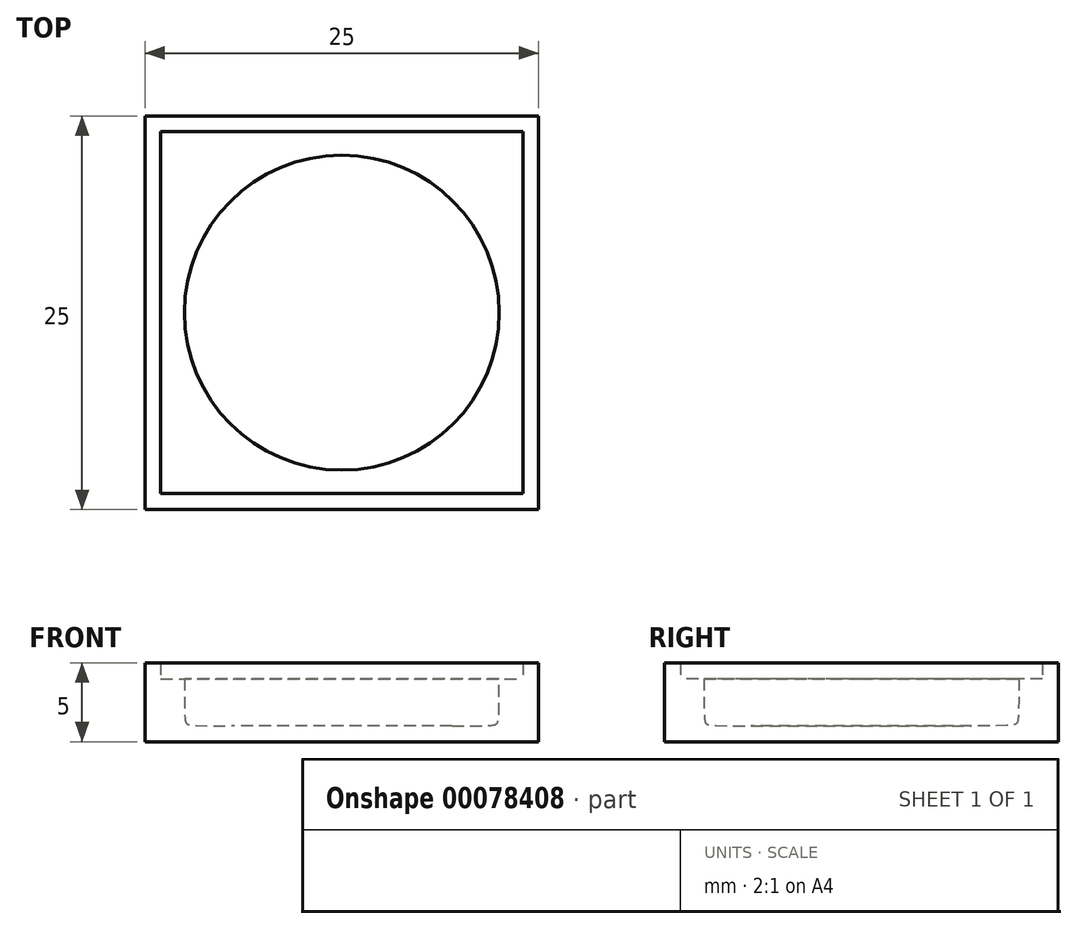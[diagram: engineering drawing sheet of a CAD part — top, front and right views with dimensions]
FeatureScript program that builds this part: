
annotation { "Feature Type Name" : "Feature", "Feature Type Description" : "" }
export const myFeature = defineFeature(function(context is Context, id is Id, definition is map)
    precondition{}
    {
        {
            var Q0;
            Q0=qCreatedBy(makeId("Top.planeOp"),FACE);
            var sketch = newSketch(context, id + "F0", { "sketchPlane" : qUnion([Q0])});
            skLineSegment(sketch, "E0.bottom", {"start": v(-11.5, 11.5) * mm, "end": v(11.5, 11.5) * mm});
            skLineSegment(sketch, "E0.top", {"start": v(-11.5, -11.5) * mm, "end": v(11.5, -11.5) * mm});
            skLineSegment(sketch, "E0.left", {"start": v(-11.5, 11.5) * mm, "end": v(-11.5, -11.5) * mm});
            skLineSegment(sketch, "E0.right", {"start": v(11.5, 11.5) * mm, "end": v(11.5, -11.5) * mm});
            skPoint(sketch, "E0.middle", {"position": v(0, 0) * mm});
            skCircle(sketch, "E1", {"center": v(0, 0) * mm, "radius": 10 * mm});
            skLineSegment(sketch, "E2.bottom", {"start": v(-12.5, 12.5) * mm, "end": v(12.5, 12.5) * mm});
            skLineSegment(sketch, "E2.top", {"start": v(-12.5, -12.5) * mm, "end": v(12.5, -12.5) * mm});
            skLineSegment(sketch, "E2.left", {"start": v(-12.5, 12.5) * mm, "end": v(-12.5, -12.5) * mm});
            skLineSegment(sketch, "E2.right", {"start": v(12.5, 12.5) * mm, "end": v(12.5, -12.5) * mm});
            skSolve(sketch);
        }
        {
            var Q0;
            Q0=makeQuery(id+"F0.imprint","IMPRINT",FACE,{"disambiguationData":[TD([[makeQuery(id+"F0.imprint","IMPRINT",EDGE,{"derivedFrom":sQuery(id+"F0.wireOp",EDGE,"E1")}),1.0]])]});
            var Q1;
            Q1=makeQuery(id+"F0.imprint","IMPRINT",FACE,{"disambiguationData":[TD([[makeQuery(id+"F0.imprint","IMPRINT",EDGE,{"derivedFrom":sQuery(id+"F0.wireOp",EDGE,"E0.bottom")}),-1.0]])]});
            var Q2;
            Q2=makeQuery(id+"F0.imprint","IMPRINT",FACE,{"disambiguationData":[TD([[makeQuery(id+"F0.imprint","IMPRINT",EDGE,{"derivedFrom":sQuery(id+"F0.wireOp",EDGE,"E0.bottom")}),1.0]])]});
            extrude(context, id + "F1", {"entities" : qUnion([Q0, Q1, Q2]), "oppositeDirection" : true, "depth" : 1 * mm, "offsetDistance" : 25 * mm});
        }
        {
            var Q0;
            Q0=makeQuery(id+"F0.imprint","IMPRINT",FACE,{"disambiguationData":[TD([[makeQuery(id+"F0.imprint","IMPRINT",EDGE,{"derivedFrom":sQuery(id+"F0.wireOp",EDGE,"E0.bottom")}),-1.0]])]});
            extrude(context, id + "F2", {"entities" : qUnion([Q0]), "operationType" : NewBodyOperationType.ADD, "depth" : 3 * mm, "offsetDistance" : 25 * mm});
        }
        {
            var Q0;
            Q0=makeQuery(id+"F0.imprint","IMPRINT",FACE,{"disambiguationData":[TD([[makeQuery(id+"F0.imprint","IMPRINT",EDGE,{"derivedFrom":sQuery(id+"F0.wireOp",EDGE,"E0.bottom")}),1.0]])]});
            extrude(context, id + "F3", {"entities" : qUnion([Q0]), "operationType" : NewBodyOperationType.ADD, "depth" : 4 * mm, "offsetDistance" : 25 * mm});
        }
        {
            var Q0;
            Q0=makeQuery(id+"F2.boolean.opBoolean","SPLIT",FACE,{"disambiguationData":[TD([makeQuery(id+"F2.opExtrude","SWEPT_FACE",FACE,{"disambiguationData":[OSD([sQuery(id+"F0.wireOp",EDGE,"E1")])]})])],"derivedFrom":makeQuery(id+"F1.opExtrude","CAP_FACE",FACE,{"disambiguationData":[OSD([sQuery(id+"F0.wireOp",EDGE,"E2.bottom"),sQuery(id+"F0.wireOp",EDGE,"E2.top"),sQuery(id+"F0.wireOp",EDGE,"E2.left"),sQuery(id+"F0.wireOp",EDGE,"E2.right")])],"isStart":true})});
            var Q1;
            Q1=makeQuery(id+"F2.opExtrude","CAP_EDGE",EDGE,{"disambiguationData":[OSD([sQuery(id+"F0.wireOp",EDGE,"E1")])],"isStart":true});
            fillet(context, id + "F4", {"entities" : qUnion([Q0, Q1]), "radius" : 3 * mm, "tangentPropagation" : true, "rho" : 0.9, "crossSection" : FilletCrossSection.CONIC, "allowEdgeOverflow" : false});
        }
    });
